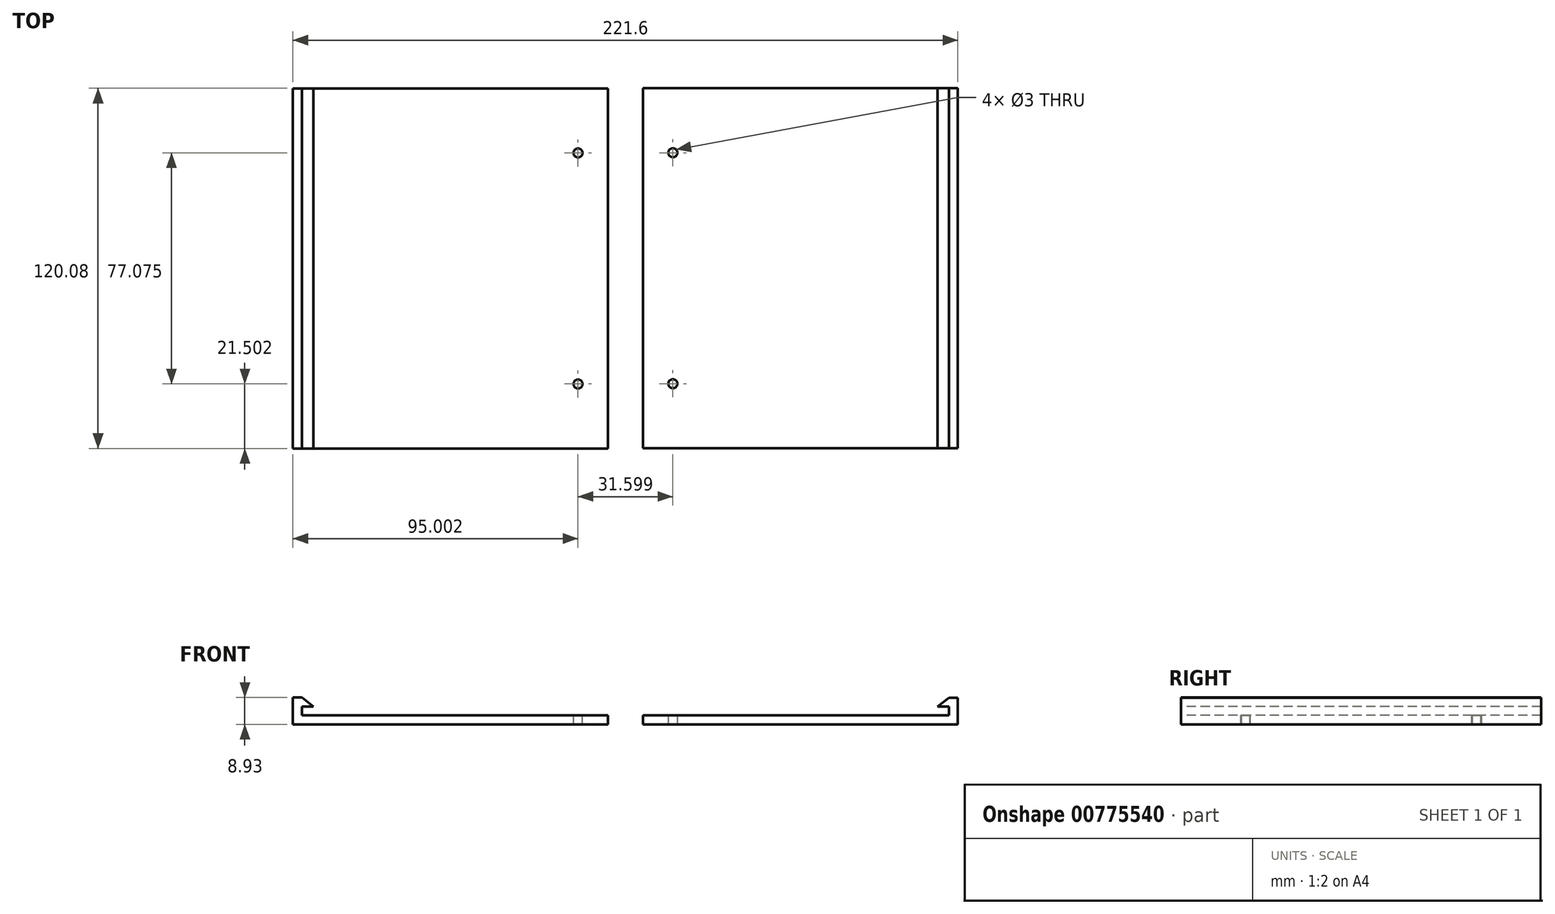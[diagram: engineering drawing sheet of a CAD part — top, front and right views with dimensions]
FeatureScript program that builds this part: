
annotation { "Feature Type Name" : "Feature", "Feature Type Description" : "" }
export const myFeature = defineFeature(function(context is Context, id is Id, definition is map)
    precondition{}
    {
        {
            var Q0;
            Q0=qCreatedBy(makeId("Top.planeOp"),FACE);
            var sketch = newSketch(context, id + "F0", { "sketchPlane" : qUnion([Q0])});
            skLineSegment(sketch, "E0.bottom", {"start": v(-83.48, 42.05) * mm, "end": v(21.52, 42.05) * mm});
            skLineSegment(sketch, "E0.top", {"start": v(-83.48, -77.95) * mm, "end": v(21.52, -77.95) * mm});
            skLineSegment(sketch, "E0.left", {"start": v(-83.48, 42.05) * mm, "end": v(-83.48, -77.95) * mm});
            skLineSegment(sketch, "E0.right", {"start": v(21.52, 42.05) * mm, "end": v(21.52, -77.95) * mm});
            skSolve(sketch);
        }
        {
            var Q0;
            Q0=makeQuery(id+"F0.imprint","IMPRINT",FACE,{"disambiguationData":[TD([[makeQuery(id+"F0.imprint","IMPRINT",EDGE,{"derivedFrom":sQuery(id+"F0.wireOp",EDGE,"E0.bottom")}),-1.0]])]});
            extrude(context, id + "F1", {"entities" : qUnion([Q0]), "depth" : (3) * mm, "offsetDistance" : 25 * mm});
        }
        {
            var Q0;
            Q0=makeQuery(id+"F1.opExtrude","CAP_FACE",FACE,{"disambiguationData":[OSD([sQuery(id+"F0.wireOp",EDGE,"E0.bottom"),sQuery(id+"F0.wireOp",EDGE,"E0.top"),sQuery(id+"F0.wireOp",EDGE,"E0.left"),sQuery(id+"F0.wireOp",EDGE,"E0.right")])],"isStart":false});
            var sketch = newSketch(context, id + "F2", { "sketchPlane" : qUnion([Q0])});
            skCircle(sketch, "E1", {"center": v(11.52, 20.55) * mm, "radius": 1.5 * mm});
            skCircle(sketch, "E2", {"center": v(11.52, -56.45) * mm, "radius": 1.5 * mm});
            skSolve(sketch);
        }
        {
            var Q0;
            Q0=makeQuery(id+"F2.imprint","IMPRINT",FACE,{"disambiguationData":[TD([[makeQuery(id+"F2.imprint","IMPRINT",EDGE,{"derivedFrom":sQuery(id+"F2.wireOp",EDGE,"E1")}),1.0]])]});
            var Q1;
            Q1=makeQuery(id+"F2.imprint","IMPRINT",FACE,{"disambiguationData":[TD([[makeQuery(id+"F2.imprint","IMPRINT",EDGE,{"derivedFrom":sQuery(id+"F2.wireOp",EDGE,"E2")}),1.0]])]});
            var Q2;
            Q2=makeQuery(id+"F1.opExtrude","CAP_FACE",FACE,{"disambiguationData":[OSD([sQuery(id+"F0.wireOp",EDGE,"E0.bottom"),sQuery(id+"F0.wireOp",EDGE,"E0.top"),sQuery(id+"F0.wireOp",EDGE,"E0.left"),sQuery(id+"F0.wireOp",EDGE,"E0.right")])],"isStart":true});
            extrude(context, id + "F3", {"entities" : qUnion([Q0, Q1]), "operationType" : NewBodyOperationType.REMOVE, "endBound" : BoundingType.UP_TO_SURFACE, "oppositeDirection" : true, "depth" : 25 * mm, "endBoundEntityFace" : qUnion([Q2]), "offsetDistance" : 25 * mm});
        }
        {
            var Q0;
            Q0=makeQuery(id+"F1.opExtrude","SWEPT_FACE",FACE,{"disambiguationData":[OSD([sQuery(id+"F0.wireOp",EDGE,"E0.top")])]});
            var sketch = newSketch(context, id + "F4", { "sketchPlane" : qUnion([Q0])});
            skLineSegment(sketch, "E3", {"start": v(-83.48, 3) * mm, "end": v(-83.48, 8.93) * mm});
            skLineSegment(sketch, "E4", {"start": v(-83.48, 8.93) * mm, "end": v(-80.52, 8.93) * mm});
            skLineSegment(sketch, "E5", {"start": v(-80.52, 8.93) * mm, "end": v(-76.64, 5.96) * mm});
            skPoint(sketch, "E5.endSnap0", {"position": v(-83.48, 5.96) * mm});
            skLineSegment(sketch, "E6", {"start": v(-76.64, 5.96) * mm, "end": v(-80.52, 5.96) * mm});
            skLineSegment(sketch, "E7", {"start": v(-80.52, 5.96) * mm, "end": v(-80.52, 3) * mm});
            skLineSegment(sketch, "E8", {"start": v(-80.52, 3) * mm, "end": v(-83.48, 3) * mm});
            skSolve(sketch);
        }
        {
            var Q0;
            Q0=makeQuery(id+"F4.imprint","IMPRINT",FACE,{"disambiguationData":[TD([[makeQuery(id+"F4.imprint","IMPRINT",EDGE,{"derivedFrom":sQuery(id+"F4.wireOp",EDGE,"E3")}),-1.0]])]});
            var Q1;
            Q1=makeQuery(id+"F1.opExtrude","SWEPT_FACE",FACE,{"disambiguationData":[OSD([sQuery(id+"F0.wireOp",EDGE,"E0.bottom")])]});
            extrude(context, id + "F5", {"entities" : qUnion([Q0]), "operationType" : NewBodyOperationType.ADD, "endBound" : BoundingType.UP_TO_SURFACE, "oppositeDirection" : true, "depth" : 25 * mm, "endBoundEntityFace" : qUnion([Q1]), "offsetDistance" : 25 * mm});
        }
        {
            var Q0;
            Q0=qCreatedBy(makeId("Top.planeOp"),FACE);
            var sketch = newSketch(context, id + "F6", { "sketchPlane" : qUnion([Q0])});
            skLineSegment(sketch, "E9.bottom", {"start": v(33.12, 42.13) * mm, "end": v(138.12, 42.13) * mm});
            skLineSegment(sketch, "E9.top", {"start": v(33.12, -77.87) * mm, "end": v(138.12, -77.87) * mm});
            skLineSegment(sketch, "E9.left", {"start": v(33.12, 42.13) * mm, "end": v(33.12, -77.87) * mm});
            skLineSegment(sketch, "E9.right", {"start": v(138.12, 42.13) * mm, "end": v(138.12, -77.87) * mm});
            skSolve(sketch);
        }
        {
            var Q0;
            Q0=makeQuery(id+"F6.imprint","IMPRINT",FACE,{"disambiguationData":[TD([[makeQuery(id+"F6.imprint","IMPRINT",EDGE,{"derivedFrom":sQuery(id+"F6.wireOp",EDGE,"E9.bottom")}),-1.0]])]});
            var sketch = newSketch(context, id + "F7", { "sketchPlane" : qUnion([Q0])});
            skCircle(sketch, "E10", {"center": v(43.12, 20.63) * mm, "radius": 1.5 * mm});
            skCircle(sketch, "E11", {"center": v(43.12, -56.37) * mm, "radius": 1.5 * mm});
            skSolve(sketch);
        }
        {
            var Q0;
            Q0=makeQuery(id+"F6.imprint","IMPRINT",FACE,{"disambiguationData":[TD([[makeQuery(id+"F6.imprint","IMPRINT",EDGE,{"derivedFrom":sQuery(id+"F6.wireOp",EDGE,"E9.bottom")}),-1.0]])]});
            extrude(context, id + "F8", {"entities" : qUnion([Q0]), "depth" : (3) * mm, "offsetDistance" : 25 * mm});
        }
        {
            var Q0;
            Q0=makeQuery(id+"F7.imprint","IMPRINT",FACE,{"disambiguationData":[TD([[makeQuery(id+"F7.imprint","IMPRINT",EDGE,{"derivedFrom":sQuery(id+"F7.wireOp",EDGE,"E10")}),1.0]])]});
            var Q1;
            Q1=makeQuery(id+"F7.imprint","IMPRINT",FACE,{"disambiguationData":[TD([[makeQuery(id+"F7.imprint","IMPRINT",EDGE,{"derivedFrom":sQuery(id+"F7.wireOp",EDGE,"E11")}),1.0]])]});
            var Q2;
            Q2=makeQuery(id+"F8.opExtrude","CAP_FACE",FACE,{"disambiguationData":[OSD([sQuery(id+"F6.wireOp",EDGE,"E9.bottom"),sQuery(id+"F6.wireOp",EDGE,"E9.top"),sQuery(id+"F6.wireOp",EDGE,"E9.left"),sQuery(id+"F6.wireOp",EDGE,"E9.right")])],"isStart":false});
            extrude(context, id + "F9", {"entities" : qUnion([Q0, Q1]), "operationType" : NewBodyOperationType.REMOVE, "endBound" : BoundingType.UP_TO_SURFACE, "depth" : 25 * mm, "endBoundEntityFace" : qUnion([Q2]), "offsetDistance" : 25 * mm});
        }
        {
            var Q0;
            Q0=makeQuery(id+"F8.opExtrude","SWEPT_FACE",FACE,{"disambiguationData":[OSD([sQuery(id+"F6.wireOp",EDGE,"E9.top")])]});
            var sketch = newSketch(context, id + "F10", { "sketchPlane" : qUnion([Q0])});
            skLineSegment(sketch, "E12", {"start": v(138.12, 3) * mm, "end": v(138.12, 8.9) * mm});
            skLineSegment(sketch, "E13", {"start": v(138.12, 8.9) * mm, "end": v(135.14, 8.9) * mm});
            skLineSegment(sketch, "E14", {"start": v(135.14, 8.9) * mm, "end": v(131.3, 5.95) * mm});
            skPoint(sketch, "E14.endSnap0", {"position": v(138.12, 5.95) * mm});
            skLineSegment(sketch, "E15", {"start": v(131.3, 5.95) * mm, "end": v(135.14, 5.95) * mm});
            skLineSegment(sketch, "E16", {"start": v(135.14, 5.95) * mm, "end": v(135.14, 3) * mm});
            skLineSegment(sketch, "E17", {"start": v(135.14, 3) * mm, "end": v(138.12, 3) * mm});
            skSolve(sketch);
        }
        {
            var Q0;
            Q0=makeQuery(id+"F10.imprint","IMPRINT",FACE,{"disambiguationData":[TD([[makeQuery(id+"F10.imprint","IMPRINT",EDGE,{"derivedFrom":sQuery(id+"F10.wireOp",EDGE,"E12")}),1.0]])]});
            var Q1;
            Q1=makeQuery(id+"F8.opExtrude","SWEPT_FACE",FACE,{"disambiguationData":[OSD([sQuery(id+"F6.wireOp",EDGE,"E9.bottom")])]});
            extrude(context, id + "F11", {"entities" : qUnion([Q0]), "operationType" : NewBodyOperationType.ADD, "endBound" : BoundingType.UP_TO_SURFACE, "oppositeDirection" : true, "depth" : 25 * mm, "endBoundEntityFace" : qUnion([Q1]), "offsetDistance" : 25 * mm});
        }
    });
